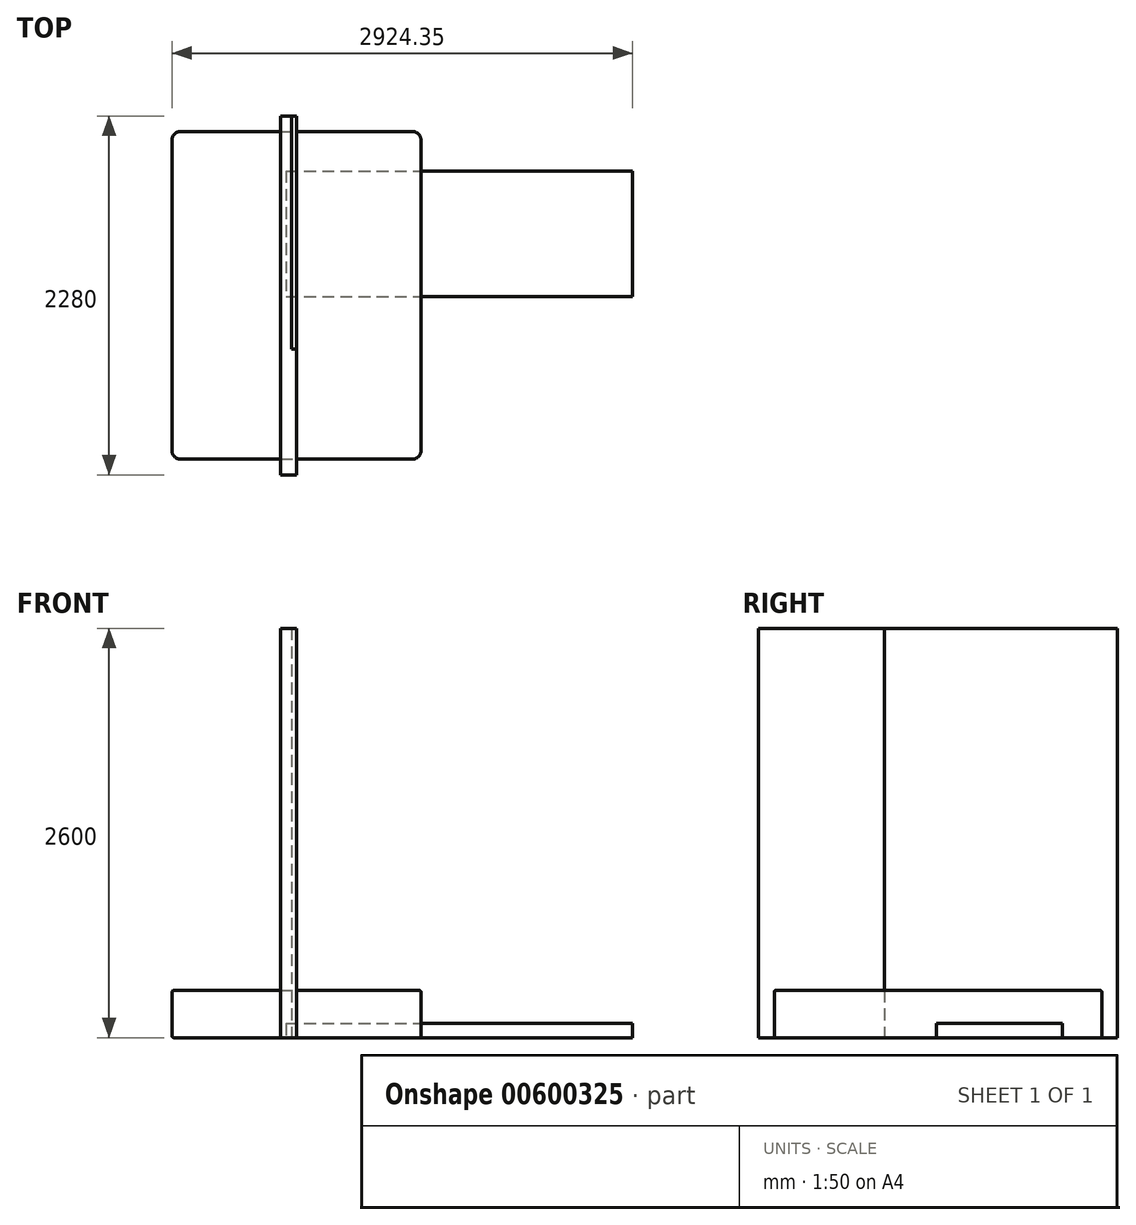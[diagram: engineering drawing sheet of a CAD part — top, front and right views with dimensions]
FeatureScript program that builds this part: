
annotation { "Feature Type Name" : "Feature", "Feature Type Description" : "" }
export const myFeature = defineFeature(function(context is Context, id is Id, definition is map)
    precondition{}
    {
        {
            var Q0;
            Q0=qCreatedBy(makeId("Top.planeOp"),FACE);
            var sketch = newSketch(context, id + "F0", { "sketchPlane" : qUnion([Q0])});
            skLineSegment(sketch, "E0.bottom", {"start": v(-790, 1040) * mm, "end": v(790, 1040) * mm});
            skLineSegment(sketch, "E0.top", {"start": v(-790, -1040) * mm, "end": v(790, -1040) * mm});
            skLineSegment(sketch, "E0.left", {"start": v(-790, 1040) * mm, "end": v(-790, -1040) * mm});
            skLineSegment(sketch, "E0.right", {"start": v(790, 1040) * mm, "end": v(790, -1040) * mm});
            skSolve(sketch);
        }
        {
            var Q0;
            Q0 = qSketchRegion(id + "F0", true);
            extrude(context, id + "F1", {"entities" : qUnion([Q0]), "depth" : 300 * mm, "offsetDistance" : 25 * mm});
        }
        {
            var Q0;
            Q0=makeQuery(id+"F1.opExtrude","SWEPT_EDGE",EDGE,{"disambiguationData":[OSD([sQuery(id+"F0.wireOp",EDGE,"E0.bottom"),sQuery(id+"F0.wireOp",EDGE,"E0.left")])]});
            var Q1;
            Q1=makeQuery(id+"F1.opExtrude","SWEPT_EDGE",EDGE,{"disambiguationData":[OSD([sQuery(id+"F0.wireOp",EDGE,"E0.top"),sQuery(id+"F0.wireOp",EDGE,"E0.left")])]});
            var Q2;
            Q2=makeQuery(id+"F1.opExtrude","SWEPT_EDGE",EDGE,{"disambiguationData":[OSD([sQuery(id+"F0.wireOp",EDGE,"E0.top"),sQuery(id+"F0.wireOp",EDGE,"E0.right")])]});
            var Q3;
            Q3=makeQuery(id+"F1.opExtrude","SWEPT_EDGE",EDGE,{"disambiguationData":[OSD([sQuery(id+"F0.wireOp",EDGE,"E0.bottom"),sQuery(id+"F0.wireOp",EDGE,"E0.right")])]});
            fillet(context, id + "F2", {"entities" : qUnion([Q0, Q1, Q2, Q3]), "radius" : 50 * mm, "tangentPropagation" : true, "allowEdgeOverflow" : false});
        }
        {
            var Q0;
            Q0=makeQuery(id+"F1.opExtrude","CAP_EDGE",EDGE,{"disambiguationData":[OSD([sQuery(id+"F0.wireOp",EDGE,"E0.left")])],"isStart":false});
            var Q1;
            Q1=makeQuery(id+"F1.opExtrude","CAP_EDGE",EDGE,{"disambiguationData":[OSD([sQuery(id+"F0.wireOp",EDGE,"E0.left")])],"isStart":true});
            fillet(context, id + "F3", {"entities" : qUnion([Q0, Q1]), "radius" : 10 * mm, "tangentPropagation" : true, "allowEdgeOverflow" : false});
        }
        {
            var Q0;
            Q0=qCreatedBy(makeId("Top.planeOp"),FACE);
            var sketch = newSketch(context, id + "F4", { "sketchPlane" : qUnion([Q0])});
            skLineSegment(sketch, "E1.bottom", {"start": v(-65.65, 790.72) * mm, "end": v(2134.35, 790.72) * mm});
            skLineSegment(sketch, "E1.top", {"start": v(-65.65, -9.28) * mm, "end": v(2134.35, -9.28) * mm});
            skLineSegment(sketch, "E1.left", {"start": v(-65.65, 790.72) * mm, "end": v(-65.65, -9.28) * mm});
            skLineSegment(sketch, "E1.right", {"start": v(2134.35, 790.72) * mm, "end": v(2134.35, -9.28) * mm});
            skSolve(sketch);
        }
        {
            var Q0;
            Q0=makeQuery(id+"F4.imprint","IMPRINT",FACE,{"disambiguationData":[TD([[makeQuery(id+"F4.imprint","IMPRINT",EDGE,{"derivedFrom":sQuery(id+"F4.wireOp",EDGE,"E1.bottom")}),-1.0]])]});
            extrude(context, id + "F5", {"entities" : qUnion([Q0]), "depth" : 90 * mm, "offsetDistance" : 25 * mm});
        }
        {
            var Q0;
            Q0=qCreatedBy(makeId("Right.planeOp"),FACE);
            var sketch = newSketch(context, id + "F6", { "sketchPlane" : qUnion([Q0])});
            skLineSegment(sketch, "E2.bottom", {"start": v(-1140, 2600) * mm, "end": v(1140, 2600) * mm});
            skLineSegment(sketch, "E2.top", {"start": v(-1140, 0) * mm, "end": v(1140, 0) * mm});
            skLineSegment(sketch, "E2.left", {"start": v(-1140, 2600) * mm, "end": v(-1140, 0) * mm});
            skLineSegment(sketch, "E2.right", {"start": v(1140, 2600) * mm, "end": v(1140, 0) * mm});
            skSolve(sketch);
        }
        {
            var Q0;
            Q0=makeQuery(id+"F6.imprint","IMPRINT",FACE,{"disambiguationData":[TD([[makeQuery(id+"F6.imprint","IMPRINT",EDGE,{"derivedFrom":sQuery(id+"F6.wireOp",EDGE,"E2.bottom")}),-1.0]])]});
            extrude(context, id + "F7", {"entities" : qUnion([Q0]), "oppositeDirection" : true, "depth" : 100 * mm, "offsetDistance" : 25 * mm});
        }
        {
            var Q0;
            Q0=qCreatedBy(makeId("Right.planeOp"),FACE);
            var sketch = newSketch(context, id + "F8", { "sketchPlane" : qUnion([Q0])});
            skLineSegment(sketch, "E3.bottom", {"start": v(1140, 2600) * mm, "end": v(-340, 2600) * mm});
            skLineSegment(sketch, "E3.top", {"start": v(1140, 0) * mm, "end": v(-340, 0) * mm});
            skLineSegment(sketch, "E3.left", {"start": v(1140, 2600) * mm, "end": v(1140, 0) * mm});
            skLineSegment(sketch, "E3.right", {"start": v(-340, 2600) * mm, "end": v(-340, 0) * mm});
            skSolve(sketch);
        }
        {
            var Q0;
            Q0 = qSketchRegion(id + "F8", true);
            extrude(context, id + "F9", {"entities" : qUnion([Q0]), "oppositeDirection" : true, "depth" : 30 * mm, "offsetDistance" : 25 * mm});
        }
    });
